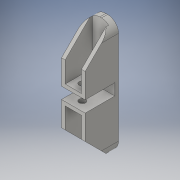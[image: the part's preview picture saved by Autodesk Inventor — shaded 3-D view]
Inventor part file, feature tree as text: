
AUTODESK INVENTOR PART (.ipt)
format: ipt  version: 2016 (Build 200138000, 138)  size: 183,808 bytes
history: native  units: in
note: dims shown in document units (in); Inventor stores cm internally (conversion verified against a paired STEP export)
features: extrude x8, sketch x8, chamfer x2, fillet x1
ambient origin geometry x8: Origin, YZ Plane, XZ Plane, XY Plane, X Axis, Y Axis, Z Axis, Center Point
bodies: Solid1 (feature_tree)
feature tree (19):
  extrude  "Extrusion1"  Depth=2.111in
  extrude  "Extrusion2"  Depth=0.95in
  extrude  "Extrusion3"  Depth=0.545in
  chamfer  "Chamfer1"  Distance=1.0in
  extrude  "Extrusion4"  Depth=0.068in
  extrude  "Extrusion5"  Depth=0.882in TaperAngle=0.0deg
  extrude  "Extrusion6"  Depth=0.545in TaperAngle=0.0deg
  chamfer  "Chamfer2"  Distance=1.545in
  extrude  "Extrusion7"  Depth=0.882in TaperAngle=0.0deg
  extrude  "Extrusion8"  Depth=0.2in
  fillet  "Fillet1"  Radius=0.1184in
  sketch  "Sketch1"  dims[d0=0.434in d1=2.111in]
  sketch  "Sketch2"  dims[d2=0.067in d3=0.0in d4=0.95in]
  sketch  "Sketch3"  dims[d5=0.545in d6=0.0in d7=0.1181in]
  sketch  "Sketch4"  dims[d8=0.1657in d9=1.0in d10=0.0in]
  sketch  "Sketch5"  dims[d11=0.5in d12=0.125in d13=45.0deg d14=0.068in]
  sketch  "Sketch6"  dims[d15=0.068in d16=0.882in d17=0.0in]
  sketch  "Sketch7"  dims[d18=0.95in d19=0.545in d20=0.0in d21=1.545in d22=0.0in]
  sketch  "Sketch8"  dims[d23=0.5in d24=0.125in d25=45.0deg d26=0.882in d27=0.0in d28=0.1181in d29=0.1184in d30=0.441in d31=0.441in d32=0.882in d33=0.0in d34=0.2in]
